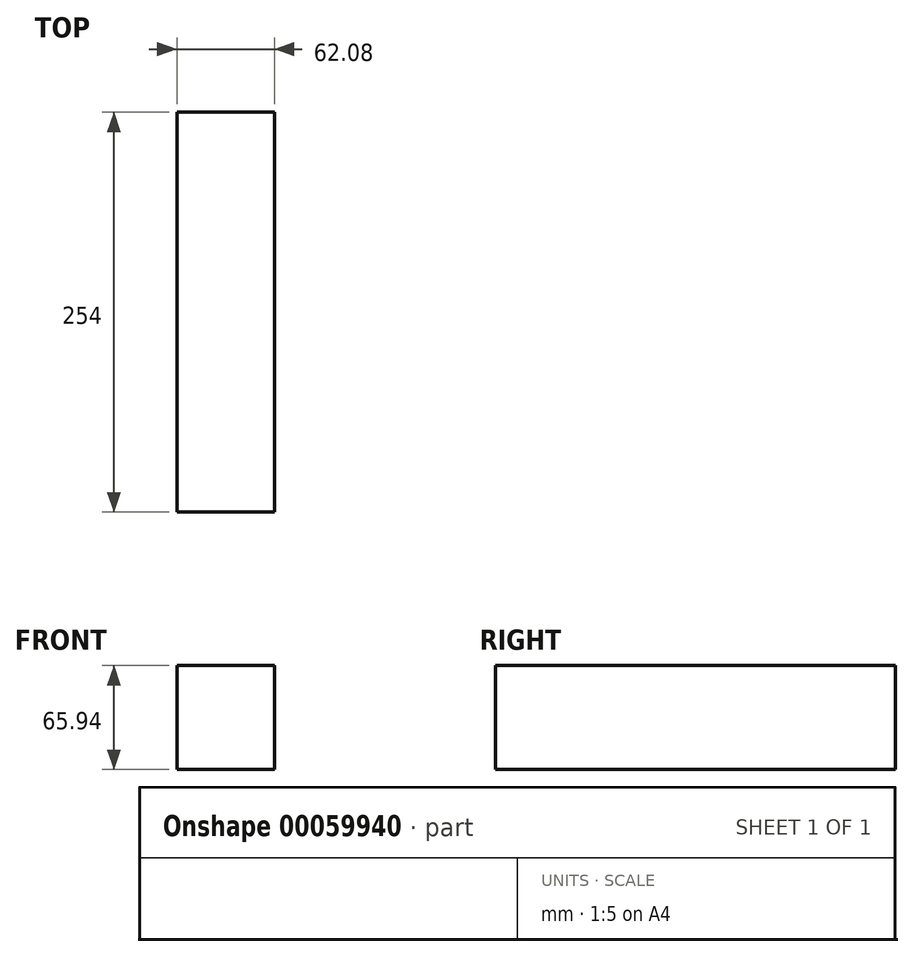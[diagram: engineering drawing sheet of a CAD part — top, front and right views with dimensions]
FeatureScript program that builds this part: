
annotation { "Feature Type Name" : "Feature", "Feature Type Description" : "" }
export const myFeature = defineFeature(function(context is Context, id is Id, definition is map)
    precondition{}
    {
        {
            var Q0;
            Q0=qCreatedBy(makeId("Front.planeOp"),FACE);
            var sketch = newSketch(context, id + "F0", { "sketchPlane" : qUnion([Q0])});
            skLineSegment(sketch, "E0.rect.bottom", {"start": v(-31.04, 32.97) * mm, "end": v(31.04, 32.97) * mm});
            skLineSegment(sketch, "E0.rect.top", {"start": v(-31.04, -32.97) * mm, "end": v(31.04, -32.97) * mm});
            skLineSegment(sketch, "E0.rect.left", {"start": v(-31.04, 32.97) * mm, "end": v(-31.04, -32.97) * mm});
            skLineSegment(sketch, "E0.rect.right", {"start": v(31.04, 32.97) * mm, "end": v(31.04, -32.97) * mm});
            skPoint(sketch, "E0.rect.middle", {"position": v(0, 0) * mm});
            skSolve(sketch);
        }
        {
            var Q0;
            Q0=makeQuery(id+"F0.imprint","IMPRINT",FACE,{"disambiguationData":[TD([[makeQuery(id+"F0.imprint","IMPRINT",EDGE,{"derivedFrom":sQuery(id+"F0.wireOp",EDGE,"E0.rect.bottom")}),-1.0]])]});
            extrude(context, id + "F1", {"entities" : qUnion([Q0]), "depth" : 254 * mm});
        }
    });
